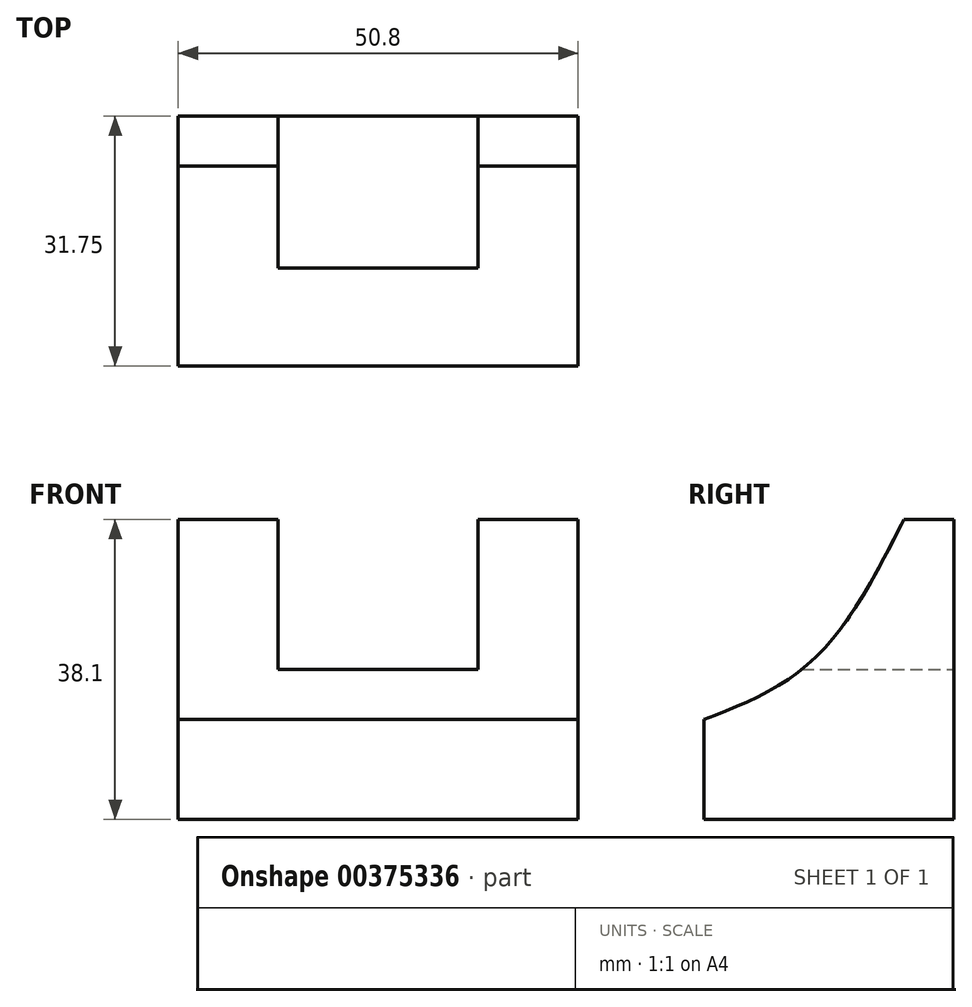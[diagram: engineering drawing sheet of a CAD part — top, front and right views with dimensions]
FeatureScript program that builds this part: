
annotation { "Feature Type Name" : "Feature", "Feature Type Description" : "" }
export const myFeature = defineFeature(function(context is Context, id is Id, definition is map)
    precondition{}
    {
        {
            var Q0;
            Q0=qCreatedBy(makeId("Right.planeOp"),FACE);
            var sketch = newSketch(context, id + "F0", { "sketchPlane" : qUnion([Q0])});
            skLineSegment(sketch, "E0", {"start": v(0, 0) * mm, "end": v(31.75, 0) * mm});
            skLineSegment(sketch, "E1", {"start": v(31.75, 0) * mm, "end": v(31.75, 38.1) * mm});
            skLineSegment(sketch, "E2", {"start": v(31.75, 38.1) * mm, "end": v(25.4, 38.1) * mm});
            skLineSegment(sketch, "E3", {"start": v(0, 0) * mm, "end": v(0, 12.7) * mm});
            skFitSpline(sketch, "E4", {"points": [v(0, 12.7) * mm, v(13.82, 20.25) * mm, v(25.4, 38.1) * mm], "startDerivative": vector(31.82, 12.41) * mm, "endDerivative": vector(19.3, 37.75) * mm});
            skSolve(sketch);
        }
        {
            var Q0;
            Q0 = qSketchRegion(id + "F0", true);
            extrude(context, id + "F1", {"entities" : qUnion([Q0]), "depth" : 50.8 * mm});
        }
        {
            var Q0;
            Q0=makeQuery(id+"F1.opExtrude","SWEPT_FACE",FACE,{"disambiguationData":[OSD([sQuery(id+"F0.wireOp",EDGE,"E1")])]});
            var sketch = newSketch(context, id + "F2", { "sketchPlane" : qUnion([Q0])});
            skLineSegment(sketch, "E5", {"start": v(-50.8, 38.1) * mm, "end": v(-38.1, 38.1) * mm});
            skLineSegment(sketch, "E6", {"start": v(-38.1, 38.1) * mm, "end": v(-38.1, 19.05) * mm});
            skLineSegment(sketch, "E7", {"start": v(-38.1, 19.05) * mm, "end": v(-12.7, 19.05) * mm});
            skLineSegment(sketch, "E8", {"start": v(-12.7, 19.05) * mm, "end": v(-12.7, 38.1) * mm});
            skLineSegment(sketch, "E9", {"start": v(-12.7, 38.1) * mm, "end": v(0, 38.1) * mm});
            skLineSegment(sketch, "E10", {"start": v(-38.1, 38.1) * mm, "end": v(-12.7, 38.1) * mm});
            skSolve(sketch);
        }
        {
            var Q0;
            Q0=makeQuery(id+"F2.imprint","IMPRINT",FACE,{"disambiguationData":[TD([[makeQuery(id+"F2.imprint","IMPRINT",EDGE,{"derivedFrom":sQuery(id+"F2.wireOp",EDGE,"E6")}),1.0]])]});
            extrude(context, id + "F3", {"entities" : qUnion([Q0]), "operationType" : NewBodyOperationType.REMOVE, "oppositeDirection" : true, "depth" : 25.4 * mm});
        }
    });
